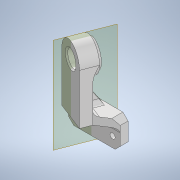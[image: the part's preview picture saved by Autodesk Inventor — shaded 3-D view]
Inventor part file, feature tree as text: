
AUTODESK INVENTOR PART (.ipt)
format: ipt  version: 2020 (Build 240168000, 168)  size: 366,080 bytes
history: native  units: mm
features: extrude x13, sketch x13, projected_geometry x13, other x5, chamfer x4, fillet x3, reference x3, plane x1
ambient origin geometry x8: Origin, YZ Plane, XZ Plane, XY Plane, X Axis, Y Axis, Z Axis, Center Point
bodies: Solid1 (feature_tree)
feature tree (55):
  extrude  "Extrusion1"  Depth=8.0mm
  extrude  "Extrusion2"  Depth=2.0mm
  extrude  "Extrusion3"  Depth=20.0mm
  extrude  "Extrusion5"  Depth=3.0mm
  extrude  "Extrusion6"  Depth=3.0mm
  extrude  "Extrusion7"  Depth=1.0mm
  extrude  "Extrusion8"  Depth=25.0mm TaperAngle=0.0deg
  extrude  "Extrusion10"  Depth=6.0mm
  extrude  "Extrusion11"  Depth=6.0mm
  plane  "Work Plane1"
  extrude  "Extrusion12"  Depth=4.5mm
  fillet  "Fillet1"  Radius=25.0mm
  fillet  "Fillet2"  Radius=25.0mm
  chamfer  "Chamfer1"  Distance=25.0mm
  chamfer  "Chamfer2"  Distance=25.0mm
  extrude  "Extrusion13"  Depth=6.0mm
  extrude  "Extrusion14"  Depth=2.0mm TaperAngle=0.0deg
  extrude  "Extrusion15"  Depth=2.0mm
  fillet  "Fillet3"  Radius=1.5mm
  chamfer  "Chamfer4"  Distance=2.0mm Angle=45.0deg
  chamfer  "Chamfer5"  Distance=2.0mm Angle=45.0deg
  sketch  "Sketch1"  dims[d0=8.0mm d1=20.0mm]
  reference  "Reference1"
  sketch  "Sketch2"  dims[d2=2.0mm d3=2.0mm]
  projected_geometry  "Projected Loop1"
  reference  "Reference2"
  sketch  "Sketch3"  dims[d4=3.0mm d5=0.0mm d6=20.0mm]
  projected_geometry  "Projected Loop2"
  sketch  "Sketch4"  dims[d7=3.0mm d8=3.0mm]
  reference  "Reference3"
  sketch  "Sketch5"  dims[d9=3.0mm d10=3.0mm]
  projected_geometry  "Projected Loop3"
  sketch  "Sketch6"  dims[d11=3.0mm d12=0.0mm d13=1.0mm]
  projected_geometry  "Projected Loop4"
  sketch  "Sketch7"  dims[d14=14.0mm d15=25.0mm d16=0.0mm]
  projected_geometry  "Projected Loop5"
  sketch  "Sketch9"  dims[d17=6.0mm d20=3.0mm]
  projected_geometry  "Projected Loop7"
  sketch  "Sketch10"  dims[d21=25.0mm d22=0.0mm d23=6.0mm]
  projected_geometry  "Projected Loop8"
  sketch  "Sketch11"  dims[d24=25.0mm d25=0.0mm d26=4.5mm d27=25.0mm d28=0.0mm d29=25.0mm d30=0.0mm]
  projected_geometry  "Projected Loop9"
  projected_geometry  "Projected Loop10"
  sketch  "Sketch12"  dims[d34=6.0mm d35=25.0mm d36=0.0mm d37=25.0mm d38=0.0mm]
  projected_geometry  "Projected Loop11"
  sketch  "Sketch13"  dims[d39=6.0mm d40=3.0mm]
  projected_geometry  "Projected Loop12"
  projected_geometry  "Projected Loop13"
  projected_geometry  "Projected Loop14"
  sketch  "Sketch14"  dims[d41=5.0mm d42=2.0mm d43=0.0mm d44=1.5mm d45=1.5mm d46=2.0mm d47=2.0mm d48=45.0deg d49=2.0mm d50=2.0mm d51=45.0deg d52=12.0mm d53=3.0mm d54=0.0mm d55=8.0mm d56=0.0mm d60=6.15mm d61=10.0mm d62=0.0mm d63=2.0mm d64=1.0mm d65=2.0mm d66=45.0deg d67=0.5mm d68=2.0mm d69=45.0deg]
  parser-record x1  (decoder bookkeeping rows leaked as tree rows — omitted from the tree; the rows remain in map.json)
  other  "body_1.iam"
  other  "leg_1:1"
  other  "leg_holder_2:1"
  other  "body_conn_1:1"
note: 1 file-system path scrubbed to <path> (originals preserved in map.json)
